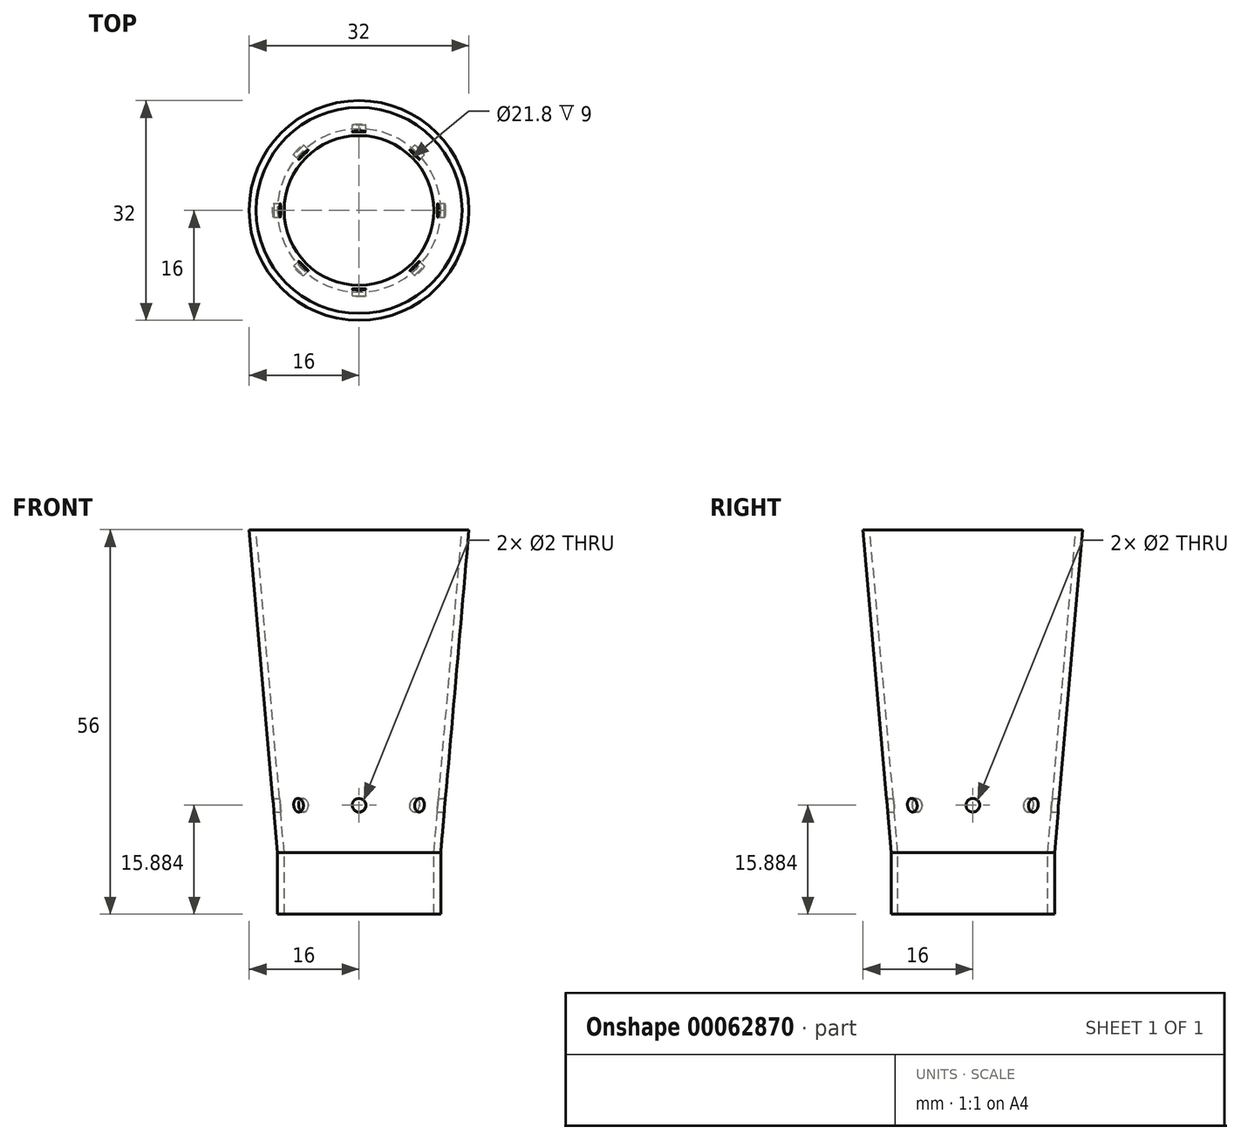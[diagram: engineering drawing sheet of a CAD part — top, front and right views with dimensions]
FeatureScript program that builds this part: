
annotation { "Feature Type Name" : "Feature", "Feature Type Description" : "" }
export const myFeature = defineFeature(function(context is Context, id is Id, definition is map)
    precondition{}
    {
        {
            var Q0;
            Q0=qCreatedBy(makeId("Front.planeOp"),FACE);
            var sketch = newSketch(context, id + "F0", { "sketchPlane" : qUnion([Q0])});
            skLineSegment(sketch, "E0", {"start": v(0, 37.58) * mm, "end": v(16, 37.58) * mm});
            skLineSegment(sketch, "E1", {"start": v(0, 37.58) * mm, "end": v(0, -9.42) * mm});
            skLineSegment(sketch, "E2", {"start": v(0, -9.42) * mm, "end": v(11.9, -9.42) * mm});
            skLineSegment(sketch, "E3", {"start": v(11.9, -9.42) * mm, "end": v(16, 37.58) * mm});
            skLineSegment(sketch, "E4", {"start": v(11.9, -9.42) * mm, "end": v(11.9, -18.42) * mm});
            skLineSegment(sketch, "E5", {"start": v(11.9, -18.42) * mm, "end": v(0, -18.42) * mm});
            skLineSegment(sketch, "E6", {"start": v(0, -18.42) * mm, "end": v(0, -9.42) * mm});
            skLineSegment(sketch, "E7", {"start": v(16, 37.58) * mm, "end": v(15, 37.58) * mm});
            skLineSegment(sketch, "E8", {"start": v(15, 37.58) * mm, "end": v(10.9, -9.42) * mm});
            skLineSegment(sketch, "E9", {"start": v(10.9, -9.42) * mm, "end": v(10.9, -18.42) * mm});
            skSolve(sketch);
        }
        {
            var Q0;
            {var subQ0=sQuery(id+"F0.wireOp",EDGE,"E3");Q0=makeQuery(id+"F0.imprint","IMPRINT",FACE,{"disambiguationData":[TD([[makeQuery(id+"F0.imprint","IMPRINT",EDGE,{"derivedFrom":subQ0}),1.0]])]});}
            var Q1;
            {var subQ0=sQuery(id+"F0.wireOp",EDGE,"E4");Q1=makeQuery(id+"F0.imprint","IMPRINT",FACE,{"disambiguationData":[TD([[makeQuery(id+"F0.imprint","IMPRINT",EDGE,{"derivedFrom":subQ0}),-1.0]])]});}
            var Q2;
            Q2=sQuery(id+"F0.wireOp",EDGE,"E1");
            revolve(context, id + "F1", {"entities" : qUnion([Q0, Q1]), "axis" : qUnion([Q2]), "revolveType" : RevolveType.FULL});
        }
        {
            var Q0;
            Q0=qCreatedBy(makeId("Front.planeOp"),FACE);
            var sketch = newSketch(context, id + "F2", { "sketchPlane" : qUnion([Q0])});
            skLineSegment(sketch, "E10", {"start": v(0, 0) * mm, "end": v(0, 37.72) * mm});
            skLineSegment(sketch, "E11", {"start": v(0, 0) * mm, "end": v(0, -9.28) * mm});
            skLineSegment(sketch, "E12", {"start": v(0, 37.72) * mm, "end": v(0, 31.01) * mm});
            skLineSegment(sketch, "E13", {"start": v(0, 31.01) * mm, "end": v(0, 24.3) * mm});
            skLineSegment(sketch, "E14", {"start": v(0, 24.3) * mm, "end": v(0, 17.6) * mm});
            skLineSegment(sketch, "E15", {"start": v(0, 17.6) * mm, "end": v(0, 10.88) * mm});
            skLineSegment(sketch, "E16", {"start": v(0, 10.88) * mm, "end": v(0, 4.17) * mm});
            skLineSegment(sketch, "E17", {"start": v(0, 4.17) * mm, "end": v(0, -2.54) * mm});
            skCircle(sketch, "E18", {"center": v(0, 31.01) * mm, "radius": 1 * mm});
            skCircle(sketch, "E19", {"center": v(0, 24.3) * mm, "radius": 1 * mm});
            skCircle(sketch, "E20", {"center": v(0, 17.6) * mm, "radius": 1 * mm});
            skCircle(sketch, "E21", {"center": v(0, 10.88) * mm, "radius": 1 * mm});
            skCircle(sketch, "E22", {"center": v(0, 4.17) * mm, "radius": 1 * mm});
            skCircle(sketch, "E23", {"center": v(0, -2.54) * mm, "radius": 1 * mm});
            skSolve(sketch);
        }
        {
            var Q0;
            {var subQ0=sQuery(id+"F2.wireOp",EDGE,"E13");var subQ1=sQuery(id+"F2.wireOp",EDGE,"E12");var subQ2=makeQuery(id+"F2.imprint","INTERSECT",VERTEX,{"derivedFrom":[subQ1,subQ0]});Q0=makeQuery(id+"F2.imprint","IMPRINT",FACE,{"disambiguationData":[TD([[makeQuery(id+"F2.imprint","IMPRINT",EDGE,{"disambiguationData":[TD([[subQ2,1.0]])],"derivedFrom":subQ1}),1.0]])]});}
            var Q1;
            {var subQ0=sQuery(id+"F2.wireOp",EDGE,"E13");var subQ1=sQuery(id+"F2.wireOp",EDGE,"E12");var subQ2=makeQuery(id+"F2.imprint","INTERSECT",VERTEX,{"derivedFrom":[subQ1,subQ0]});Q1=makeQuery(id+"F2.imprint","IMPRINT",FACE,{"disambiguationData":[TD([[makeQuery(id+"F2.imprint","IMPRINT",EDGE,{"disambiguationData":[TD([[subQ2,1.0]])],"derivedFrom":subQ1}),-1.0]])]});}
            var Q2;
            {var subQ0=sQuery(id+"F2.wireOp",EDGE,"E14");var subQ1=sQuery(id+"F2.wireOp",EDGE,"E13");var subQ2=makeQuery(id+"F2.imprint","INTERSECT",VERTEX,{"derivedFrom":[subQ1,subQ0]});Q2=makeQuery(id+"F2.imprint","IMPRINT",FACE,{"disambiguationData":[TD([[makeQuery(id+"F2.imprint","IMPRINT",EDGE,{"disambiguationData":[TD([[subQ2,1.0]])],"derivedFrom":subQ1}),1.0]])]});}
            var Q3;
            {var subQ0=sQuery(id+"F2.wireOp",EDGE,"E14");var subQ1=sQuery(id+"F2.wireOp",EDGE,"E13");var subQ2=makeQuery(id+"F2.imprint","INTERSECT",VERTEX,{"derivedFrom":[subQ1,subQ0]});Q3=makeQuery(id+"F2.imprint","IMPRINT",FACE,{"disambiguationData":[TD([[makeQuery(id+"F2.imprint","IMPRINT",EDGE,{"disambiguationData":[TD([[subQ2,1.0]])],"derivedFrom":subQ1}),-1.0]])]});}
            var Q4;
            {var subQ0=sQuery(id+"F2.wireOp",EDGE,"E15");var subQ1=sQuery(id+"F2.wireOp",EDGE,"E14");var subQ2=makeQuery(id+"F2.imprint","INTERSECT",VERTEX,{"derivedFrom":[subQ1,subQ0]});Q4=makeQuery(id+"F2.imprint","IMPRINT",FACE,{"disambiguationData":[TD([[makeQuery(id+"F2.imprint","IMPRINT",EDGE,{"disambiguationData":[TD([[subQ2,1.0]])],"derivedFrom":subQ1}),1.0]])]});}
            var Q5;
            {var subQ0=sQuery(id+"F2.wireOp",EDGE,"E15");var subQ1=sQuery(id+"F2.wireOp",EDGE,"E14");var subQ2=makeQuery(id+"F2.imprint","INTERSECT",VERTEX,{"derivedFrom":[subQ1,subQ0]});Q5=makeQuery(id+"F2.imprint","IMPRINT",FACE,{"disambiguationData":[TD([[makeQuery(id+"F2.imprint","IMPRINT",EDGE,{"disambiguationData":[TD([[subQ2,1.0]])],"derivedFrom":subQ1}),-1.0]])]});}
            var Q6;
            {var subQ0=sQuery(id+"F2.wireOp",EDGE,"E16");var subQ1=sQuery(id+"F2.wireOp",EDGE,"E15");var subQ2=makeQuery(id+"F2.imprint","INTERSECT",VERTEX,{"derivedFrom":[subQ1,subQ0]});Q6=makeQuery(id+"F2.imprint","IMPRINT",FACE,{"disambiguationData":[TD([[makeQuery(id+"F2.imprint","IMPRINT",EDGE,{"disambiguationData":[TD([[subQ2,1.0]])],"derivedFrom":subQ1}),1.0]])]});}
            var Q7;
            {var subQ0=sQuery(id+"F2.wireOp",EDGE,"E16");var subQ1=sQuery(id+"F2.wireOp",EDGE,"E15");var subQ2=makeQuery(id+"F2.imprint","INTERSECT",VERTEX,{"derivedFrom":[subQ1,subQ0]});Q7=makeQuery(id+"F2.imprint","IMPRINT",FACE,{"disambiguationData":[TD([[makeQuery(id+"F2.imprint","IMPRINT",EDGE,{"disambiguationData":[TD([[subQ2,1.0]])],"derivedFrom":subQ1}),-1.0]])]});}
            var Q8;
            {var subQ0=sQuery(id+"F2.wireOp",EDGE,"E17");var subQ1=sQuery(id+"F2.wireOp",EDGE,"E16");var subQ2=makeQuery(id+"F2.imprint","INTERSECT",VERTEX,{"derivedFrom":[subQ1,subQ0]});Q8=makeQuery(id+"F2.imprint","IMPRINT",FACE,{"disambiguationData":[TD([[makeQuery(id+"F2.imprint","IMPRINT",EDGE,{"disambiguationData":[TD([[subQ2,1.0]])],"derivedFrom":subQ1}),1.0]])]});}
            var Q9;
            {var subQ0=sQuery(id+"F2.wireOp",EDGE,"E17");var subQ1=sQuery(id+"F2.wireOp",EDGE,"E16");var subQ2=makeQuery(id+"F2.imprint","INTERSECT",VERTEX,{"derivedFrom":[subQ1,subQ0]});Q9=makeQuery(id+"F2.imprint","IMPRINT",FACE,{"disambiguationData":[TD([[makeQuery(id+"F2.imprint","IMPRINT",EDGE,{"disambiguationData":[TD([[subQ2,1.0]])],"derivedFrom":subQ1}),-1.0]])]});}
            var Q10;
            {var subQ0=sQuery(id+"F2.wireOp",EDGE,"E17");var subQ1=sQuery(id+"F2.wireOp",EDGE,"E11");var subQ2=makeQuery(id+"F2.imprint","INTERSECT",VERTEX,{"derivedFrom":[subQ1,subQ0]});Q10=makeQuery(id+"F2.imprint","IMPRINT",FACE,{"disambiguationData":[TD([[makeQuery(id+"F2.imprint","IMPRINT",EDGE,{"disambiguationData":[TD([[subQ2,-1.0]])],"derivedFrom":subQ1}),1.0]])]});}
            var Q11;
            {var subQ0=sQuery(id+"F2.wireOp",EDGE,"E17");var subQ1=sQuery(id+"F2.wireOp",EDGE,"E11");var subQ2=makeQuery(id+"F2.imprint","INTERSECT",VERTEX,{"derivedFrom":[subQ1,subQ0]});Q11=makeQuery(id+"F2.imprint","IMPRINT",FACE,{"disambiguationData":[TD([[makeQuery(id+"F2.imprint","IMPRINT",EDGE,{"disambiguationData":[TD([[subQ2,-1.0]])],"derivedFrom":subQ1}),-1.0]])]});}
            extrude(context, id + "F3", {"entities" : qUnion([Q0, Q1, Q2, Q3, Q4, Q5, Q6, Q7, Q8, Q9, Q10, Q11]), "endBound" : BoundingType.SYMMETRIC, "depth" : 50 * mm});
        }
        {
            var Q0;
            Q0=qCreatedBy(makeId("Front.planeOp"),FACE);
            var sketch = newSketch(context, id + "F4", { "sketchPlane" : qUnion([Q0])});
            skLineSegment(sketch, "E24", {"start": v(0, 51.94) * mm, "end": v(0, -34.3) * mm});
            skSolve(sketch);
        }
        {
            var Q0;
            Q0=makeQuery(id+"F3.opExtrude","SWEPT_BODY",BODY,{"disambiguationData":[OSD([sQuery(id+"F2.wireOp",EDGE,"E18")])]});
            var Q1;
            Q1=makeQuery(id+"F3.opExtrude","SWEPT_BODY",BODY,{"disambiguationData":[OSD([sQuery(id+"F2.wireOp",EDGE,"E19")])]});
            var Q2;
            Q2=makeQuery(id+"F3.opExtrude","SWEPT_BODY",BODY,{"disambiguationData":[OSD([sQuery(id+"F2.wireOp",EDGE,"E20")])]});
            var Q3;
            Q3=makeQuery(id+"F3.opExtrude","SWEPT_BODY",BODY,{"disambiguationData":[OSD([sQuery(id+"F2.wireOp",EDGE,"E21")])]});
            var Q4;
            Q4=makeQuery(id+"F3.opExtrude","SWEPT_BODY",BODY,{"disambiguationData":[OSD([sQuery(id+"F2.wireOp",EDGE,"E22")])]});
            var Q5;
            Q5=makeQuery(id+"F3.opExtrude","SWEPT_BODY",BODY,{"disambiguationData":[OSD([sQuery(id+"F2.wireOp",EDGE,"E23")])]});
            var Q6;
            Q6=sQuery(id+"F4.wireOp",EDGE,"E24");
            transform(context, id + "F5", {"entities" : qUnion([Q0, Q1, Q2, Q3, Q4, Q5]), "transformType" : TransformType.ROTATION, "transformAxis" : qUnion([Q6]), "angle" : 45 * degree, "makeCopy" : true});
        }
        {
            var Q0;
            Q0=qCreatedBy(makeId("Front.planeOp"),FACE);
            var sketch = newSketch(context, id + "F6", { "sketchPlane" : qUnion([Q0])});
            skLineSegment(sketch, "E25", {"start": v(0, 49.76) * mm, "end": v(0, -46.38) * mm});
            skSolve(sketch);
        }
        {
            var Q0;
            Q0=makeQuery(id+"F3.opExtrude","SWEPT_BODY",BODY,{"disambiguationData":[OSD([sQuery(id+"F2.wireOp",EDGE,"E18")])]});
            var Q1;
            Q1=makeQuery(id+"F3.opExtrude","SWEPT_BODY",BODY,{"disambiguationData":[OSD([sQuery(id+"F2.wireOp",EDGE,"E19")])]});
            var Q2;
            Q2=makeQuery(id+"F3.opExtrude","SWEPT_BODY",BODY,{"disambiguationData":[OSD([sQuery(id+"F2.wireOp",EDGE,"E20")])]});
            var Q3;
            Q3=makeQuery(id+"F3.opExtrude","SWEPT_BODY",BODY,{"disambiguationData":[OSD([sQuery(id+"F2.wireOp",EDGE,"E21")])]});
            var Q4;
            Q4=makeQuery(id+"F3.opExtrude","SWEPT_BODY",BODY,{"disambiguationData":[OSD([sQuery(id+"F2.wireOp",EDGE,"E22")])]});
            var Q5;
            Q5=makeQuery(id+"F3.opExtrude","SWEPT_BODY",BODY,{"disambiguationData":[OSD([sQuery(id+"F2.wireOp",EDGE,"E23")])]});
            var Q6;
            Q6=sQuery(id+"F6.wireOp",EDGE,"E25");
            transform(context, id + "F7", {"entities" : qUnion([Q0, Q1, Q2, Q3, Q4, Q5]), "transformType" : TransformType.ROTATION, "transformAxis" : qUnion([Q6]), "angle" : 90 * degree, "makeCopy" : true});
        }
        {
            var Q0;
            Q0=qCreatedBy(makeId("Front.planeOp"),FACE);
            var sketch = newSketch(context, id + "F8", { "sketchPlane" : qUnion([Q0])});
            skLineSegment(sketch, "E26", {"start": v(0, 50.97) * mm, "end": v(0, -39.62) * mm});
            skSolve(sketch);
        }
        {
            var Q0;
            Q0=makeQuery(id+"F3.opExtrude","SWEPT_BODY",BODY,{"disambiguationData":[OSD([sQuery(id+"F2.wireOp",EDGE,"E18")])]});
            var Q1;
            Q1=makeQuery(id+"F3.opExtrude","SWEPT_BODY",BODY,{"disambiguationData":[OSD([sQuery(id+"F2.wireOp",EDGE,"E19")])]});
            var Q2;
            Q2=makeQuery(id+"F3.opExtrude","SWEPT_BODY",BODY,{"disambiguationData":[OSD([sQuery(id+"F2.wireOp",EDGE,"E20")])]});
            var Q3;
            Q3=makeQuery(id+"F3.opExtrude","SWEPT_BODY",BODY,{"disambiguationData":[OSD([sQuery(id+"F2.wireOp",EDGE,"E21")])]});
            var Q4;
            Q4=makeQuery(id+"F3.opExtrude","SWEPT_BODY",BODY,{"disambiguationData":[OSD([sQuery(id+"F2.wireOp",EDGE,"E22")])]});
            var Q5;
            Q5=makeQuery(id+"F3.opExtrude","SWEPT_BODY",BODY,{"disambiguationData":[OSD([sQuery(id+"F2.wireOp",EDGE,"E23")])]});
            var Q6;
            Q6=sQuery(id+"F8.wireOp",EDGE,"E26");
            transform(context, id + "F9", {"entities" : qUnion([Q0, Q1, Q2, Q3, Q4, Q5]), "transformType" : TransformType.ROTATION, "transformAxis" : qUnion([Q6]), "angle" : 135 * degree, "makeCopy" : true});
        }
        {
            var Q0;
            Q0=makeQuery(id+"F7.opPattern","COPY",BODY,{"derivedFrom":makeQuery(id+"F3.opExtrude","SWEPT_BODY",BODY,{"disambiguationData":[OSD([sQuery(id+"F2.wireOp",EDGE,"E18")])]}),"instanceName":"1"});
            var Q1;
            Q1=makeQuery(id+"F7.opPattern","COPY",BODY,{"derivedFrom":makeQuery(id+"F3.opExtrude","SWEPT_BODY",BODY,{"disambiguationData":[OSD([sQuery(id+"F2.wireOp",EDGE,"E19")])]}),"instanceName":"1"});
            var Q2;
            Q2=makeQuery(id+"F7.opPattern","COPY",BODY,{"derivedFrom":makeQuery(id+"F3.opExtrude","SWEPT_BODY",BODY,{"disambiguationData":[OSD([sQuery(id+"F2.wireOp",EDGE,"E20")])]}),"instanceName":"1"});
            var Q3;
            Q3=makeQuery(id+"F7.opPattern","COPY",BODY,{"derivedFrom":makeQuery(id+"F3.opExtrude","SWEPT_BODY",BODY,{"disambiguationData":[OSD([sQuery(id+"F2.wireOp",EDGE,"E21")])]}),"instanceName":"1"});
            var Q4;
            Q4=makeQuery(id+"F7.opPattern","COPY",BODY,{"derivedFrom":makeQuery(id+"F3.opExtrude","SWEPT_BODY",BODY,{"disambiguationData":[OSD([sQuery(id+"F2.wireOp",EDGE,"E22")])]}),"instanceName":"1"});
            var Q5;
            Q5=makeQuery(id+"F7.opPattern","COPY",BODY,{"derivedFrom":makeQuery(id+"F3.opExtrude","SWEPT_BODY",BODY,{"disambiguationData":[OSD([sQuery(id+"F2.wireOp",EDGE,"E23")])]}),"instanceName":"1"});
            var Q6;
            Q6=makeQuery(id+"F3.opExtrude","SWEPT_BODY",BODY,{"disambiguationData":[OSD([sQuery(id+"F2.wireOp",EDGE,"E23")])]});
            var Q7;
            Q7=makeQuery(id+"F3.opExtrude","SWEPT_BODY",BODY,{"disambiguationData":[OSD([sQuery(id+"F2.wireOp",EDGE,"E22")])]});
            var Q8;
            Q8=makeQuery(id+"F3.opExtrude","SWEPT_BODY",BODY,{"disambiguationData":[OSD([sQuery(id+"F2.wireOp",EDGE,"E21")])]});
            var Q9;
            Q9=makeQuery(id+"F3.opExtrude","SWEPT_BODY",BODY,{"disambiguationData":[OSD([sQuery(id+"F2.wireOp",EDGE,"E20")])]});
            var Q10;
            Q10=makeQuery(id+"F3.opExtrude","SWEPT_BODY",BODY,{"disambiguationData":[OSD([sQuery(id+"F2.wireOp",EDGE,"E19")])]});
            var Q11;
            Q11=makeQuery(id+"F3.opExtrude","SWEPT_BODY",BODY,{"disambiguationData":[OSD([sQuery(id+"F2.wireOp",EDGE,"E18")])]});
            var Q12;
            Q12=makeQuery(id+"F9.opPattern","COPY",BODY,{"derivedFrom":makeQuery(id+"F3.opExtrude","SWEPT_BODY",BODY,{"disambiguationData":[OSD([sQuery(id+"F2.wireOp",EDGE,"E18")])]}),"instanceName":"1"});
            var Q13;
            Q13=makeQuery(id+"F9.opPattern","COPY",BODY,{"derivedFrom":makeQuery(id+"F3.opExtrude","SWEPT_BODY",BODY,{"disambiguationData":[OSD([sQuery(id+"F2.wireOp",EDGE,"E19")])]}),"instanceName":"1"});
            var Q14;
            Q14=makeQuery(id+"F9.opPattern","COPY",BODY,{"derivedFrom":makeQuery(id+"F3.opExtrude","SWEPT_BODY",BODY,{"disambiguationData":[OSD([sQuery(id+"F2.wireOp",EDGE,"E20")])]}),"instanceName":"1"});
            var Q15;
            Q15=makeQuery(id+"F9.opPattern","COPY",BODY,{"derivedFrom":makeQuery(id+"F3.opExtrude","SWEPT_BODY",BODY,{"disambiguationData":[OSD([sQuery(id+"F2.wireOp",EDGE,"E21")])]}),"instanceName":"1"});
            var Q16;
            Q16=makeQuery(id+"F9.opPattern","COPY",BODY,{"derivedFrom":makeQuery(id+"F3.opExtrude","SWEPT_BODY",BODY,{"disambiguationData":[OSD([sQuery(id+"F2.wireOp",EDGE,"E22")])]}),"instanceName":"1"});
            var Q17;
            Q17=makeQuery(id+"F9.opPattern","COPY",BODY,{"derivedFrom":makeQuery(id+"F3.opExtrude","SWEPT_BODY",BODY,{"disambiguationData":[OSD([sQuery(id+"F2.wireOp",EDGE,"E23")])]}),"instanceName":"1"});
            var Q18;
            Q18=makeQuery(id+"F5.opPattern","COPY",BODY,{"derivedFrom":makeQuery(id+"F3.opExtrude","SWEPT_BODY",BODY,{"disambiguationData":[OSD([sQuery(id+"F2.wireOp",EDGE,"E18")])]}),"instanceName":"1"});
            var Q19;
            Q19=makeQuery(id+"F5.opPattern","COPY",BODY,{"derivedFrom":makeQuery(id+"F3.opExtrude","SWEPT_BODY",BODY,{"disambiguationData":[OSD([sQuery(id+"F2.wireOp",EDGE,"E19")])]}),"instanceName":"1"});
            var Q20;
            Q20=makeQuery(id+"F5.opPattern","COPY",BODY,{"derivedFrom":makeQuery(id+"F3.opExtrude","SWEPT_BODY",BODY,{"disambiguationData":[OSD([sQuery(id+"F2.wireOp",EDGE,"E20")])]}),"instanceName":"1"});
            var Q21;
            Q21=makeQuery(id+"F5.opPattern","COPY",BODY,{"derivedFrom":makeQuery(id+"F3.opExtrude","SWEPT_BODY",BODY,{"disambiguationData":[OSD([sQuery(id+"F2.wireOp",EDGE,"E21")])]}),"instanceName":"1"});
            var Q22;
            Q22=makeQuery(id+"F5.opPattern","COPY",BODY,{"derivedFrom":makeQuery(id+"F3.opExtrude","SWEPT_BODY",BODY,{"disambiguationData":[OSD([sQuery(id+"F2.wireOp",EDGE,"E22")])]}),"instanceName":"1"});
            var Q23;
            Q23=makeQuery(id+"F5.opPattern","COPY",BODY,{"derivedFrom":makeQuery(id+"F3.opExtrude","SWEPT_BODY",BODY,{"disambiguationData":[OSD([sQuery(id+"F2.wireOp",EDGE,"E23")])]}),"instanceName":"1"});
            var Q24;
            Q24=makeQuery(id+"F1.opRevolve","SWEPT_BODY",BODY,{"disambiguationData":[OSD([sQuery(id+"F0.wireOp",EDGE,"E3"),sQuery(id+"F0.wireOp",EDGE,"E4"),sQuery(id+"F0.wireOp",EDGE,"E5"),sQuery(id+"F0.wireOp",EDGE,"E7"),sQuery(id+"F0.wireOp",EDGE,"E8"),sQuery(id+"F0.wireOp",EDGE,"E9")])]});
            booleanBodies(context, id + "F10", {"operationType" : BooleanOperationType.SUBTRACTION, "tools" : qUnion([Q0, Q1, Q2, Q3, Q4, Q5, Q6, Q7, Q8, Q9, Q10, Q11, Q12, Q13, Q14, Q15, Q16, Q17, Q18, Q19, Q20, Q21, Q22, Q23]), "targets" : qUnion([Q24])});
        }
    });
